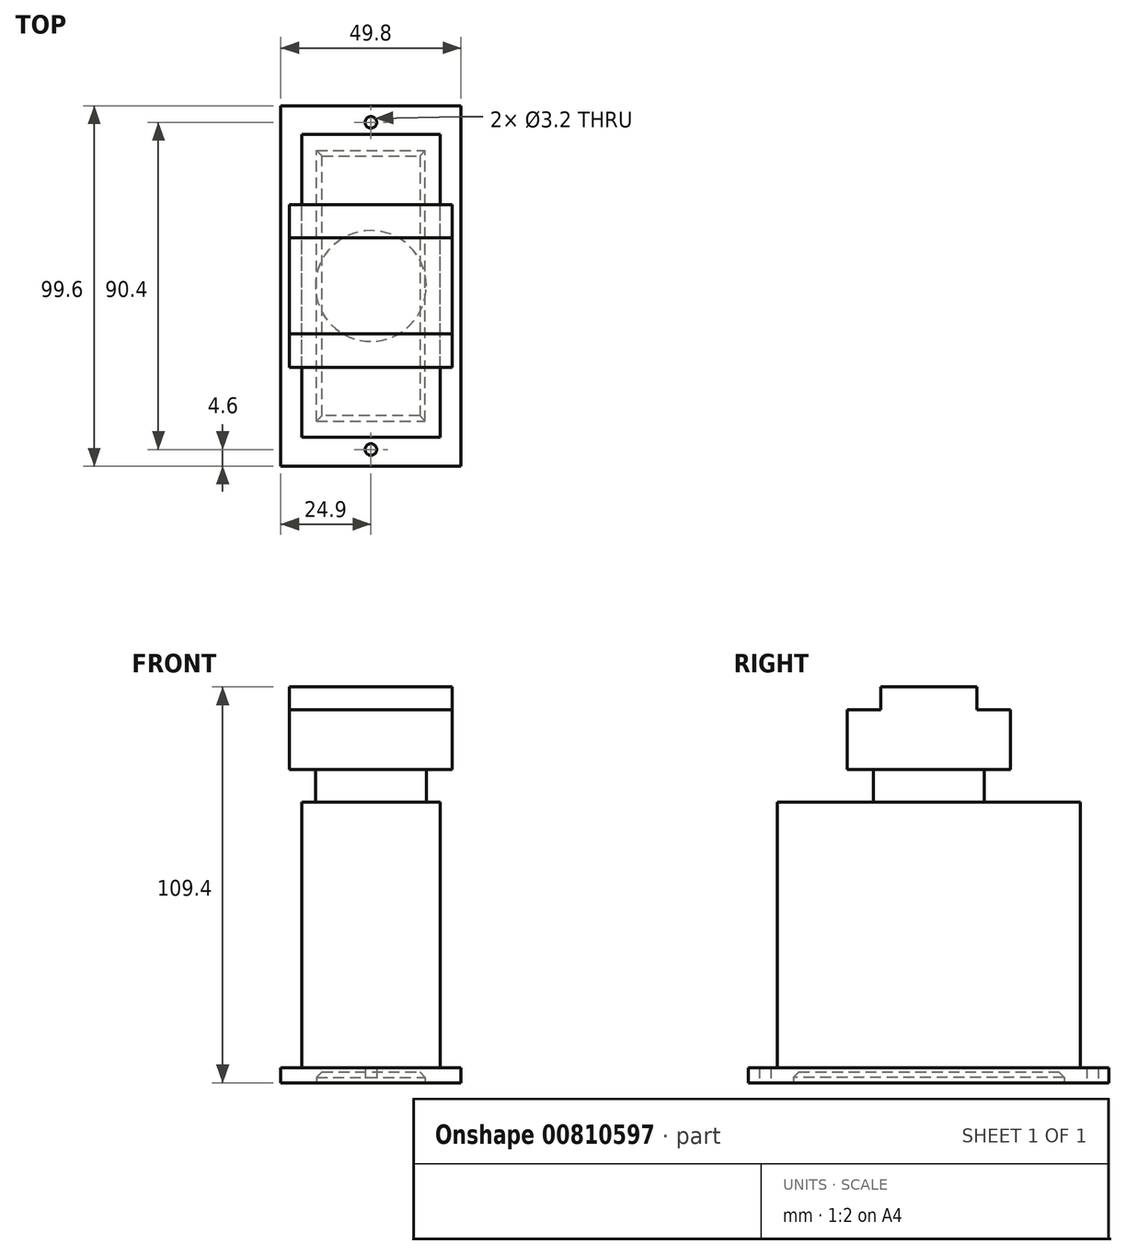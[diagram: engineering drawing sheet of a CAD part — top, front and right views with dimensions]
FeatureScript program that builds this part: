
annotation { "Feature Type Name" : "Feature", "Feature Type Description" : "" }
export const myFeature = defineFeature(function(context is Context, id is Id, definition is map)
    precondition{}
    {
        {
            var Q0;
            Q0=qCreatedBy(makeId("Top.planeOp"),FACE);
            var sketch = newSketch(context, id + "F0", { "sketchPlane" : qUnion([Q0])});
            skLineSegment(sketch, "E0.bottom", {"start": v(24.9, -49.8) * mm, "end": v(-24.9, -49.8) * mm});
            skLineSegment(sketch, "E0.top", {"start": v(24.9, 49.8) * mm, "end": v(-24.9, 49.8) * mm});
            skLineSegment(sketch, "E0.left", {"start": v(24.9, -49.8) * mm, "end": v(24.9, 49.8) * mm});
            skLineSegment(sketch, "E0.right", {"start": v(-24.9, -49.8) * mm, "end": v(-24.9, 49.8) * mm});
            skPoint(sketch, "E0.middle", {"position": v(0, 0) * mm});
            skSolve(sketch);
        }
        {
            var Q0;
            Q0 = qSketchRegion(id + "F0", true);
            extrude(context, id + "F1", {"entities" : qUnion([Q0]), "depth" : 4.2 * mm, "offsetDistance" : 25 * mm});
        }
        {
            var Q0;
            Q0=makeQuery(id+"F1.opExtrude","CAP_FACE",FACE,{"disambiguationData":[OSD([sQuery(id+"F0.wireOp",EDGE,"E0.bottom"),sQuery(id+"F0.wireOp",EDGE,"E0.top"),sQuery(id+"F0.wireOp",EDGE,"E0.left"),sQuery(id+"F0.wireOp",EDGE,"E0.right")])],"isStart":false});
            var sketch = newSketch(context, id + "F2", { "sketchPlane" : qUnion([Q0])});
            skLineSegment(sketch, "E1.bottom", {"start": v(19.12, -41.85) * mm, "end": v(-19.13, -41.85) * mm});
            skLineSegment(sketch, "E1.top", {"start": v(19.13, 41.85) * mm, "end": v(-19.12, 41.85) * mm});
            skLineSegment(sketch, "E1.left", {"start": v(19.12, -41.85) * mm, "end": v(19.13, 41.85) * mm});
            skLineSegment(sketch, "E1.right", {"start": v(-19.13, -41.85) * mm, "end": v(-19.12, 41.85) * mm});
            skPoint(sketch, "E1.middle", {"position": v(0, 0) * mm});
            skSolve(sketch);
        }
        {
            var Q0;
            Q0 = qSketchRegion(id + "F2", true);
            extrude(context, id + "F3", {"entities" : qUnion([Q0]), "operationType" : NewBodyOperationType.ADD, "depth" : 73.4 * mm, "offsetDistance" : 25 * mm});
        }
        {
            var Q0;
            Q0=makeQuery(id+"F3.opExtrude","CAP_FACE",FACE,{"disambiguationData":[OSD([sQuery(id+"F2.wireOp",EDGE,"E1.bottom"),sQuery(id+"F2.wireOp",EDGE,"E1.top"),sQuery(id+"F2.wireOp",EDGE,"E1.left"),sQuery(id+"F2.wireOp",EDGE,"E1.right")])],"isStart":false});
            var sketch = newSketch(context, id + "F4", { "sketchPlane" : qUnion([Q0])});
            skCircle(sketch, "E2", {"center": v(0, 0) * mm, "radius": 15.3 * mm});
            skSolve(sketch);
        }
        {
            var Q0;
            Q0 = qSketchRegion(id + "F4", true);
            extrude(context, id + "F5", {"entities" : qUnion([Q0]), "operationType" : NewBodyOperationType.ADD, "depth" : 9 * mm, "offsetDistance" : 25 * mm});
        }
        {
            var Q0;
            Q0=makeQuery(id+"F5.opExtrude","CAP_FACE",FACE,{"disambiguationData":[OSD([sQuery(id+"F4.wireOp",EDGE,"E2")])],"isStart":false});
            var sketch = newSketch(context, id + "F6", { "sketchPlane" : qUnion([Q0])});
            skLineSegment(sketch, "E3.bottom", {"start": v(22.5, -22.5) * mm, "end": v(-22.5, -22.5) * mm});
            skLineSegment(sketch, "E3.top", {"start": v(22.5, 22.5) * mm, "end": v(-22.5, 22.5) * mm});
            skLineSegment(sketch, "E3.left", {"start": v(22.5, -22.5) * mm, "end": v(22.5, 22.5) * mm});
            skLineSegment(sketch, "E3.right", {"start": v(-22.5, -22.5) * mm, "end": v(-22.5, 22.5) * mm});
            skPoint(sketch, "E3.middle", {"position": v(0, 0) * mm});
            skSolve(sketch);
        }
        {
            var Q0;
            Q0 = qSketchRegion(id + "F6", true);
            extrude(context, id + "F7", {"entities" : qUnion([Q0]), "depth" : 16.5 * mm, "offsetDistance" : 25 * mm});
        }
        {
            var Q0;
            Q0=makeQuery(id+"F7.opExtrude","CAP_FACE",FACE,{"disambiguationData":[OSD([sQuery(id+"F6.wireOp",EDGE,"E3.bottom"),sQuery(id+"F6.wireOp",EDGE,"E3.top"),sQuery(id+"F6.wireOp",EDGE,"E3.left"),sQuery(id+"F6.wireOp",EDGE,"E3.right")])],"isStart":false});
            var sketch = newSketch(context, id + "F8", { "sketchPlane" : qUnion([Q0])});
            skLineSegment(sketch, "E4.bottom", {"start": v(22.5, -13.25) * mm, "end": v(-22.5, -13.25) * mm});
            skLineSegment(sketch, "E4.top", {"start": v(22.5, 13.25) * mm, "end": v(-22.5, 13.25) * mm});
            skLineSegment(sketch, "E4.left", {"start": v(22.5, -13.25) * mm, "end": v(22.5, 13.25) * mm});
            skLineSegment(sketch, "E4.right", {"start": v(-22.5, -13.25) * mm, "end": v(-22.5, 13.25) * mm});
            skPoint(sketch, "E4.middle", {"position": v(0, 0) * mm});
            skSolve(sketch);
        }
        {
            var Q0;
            Q0 = qSketchRegion(id + "F8", true);
            extrude(context, id + "F9", {"entities" : qUnion([Q0]), "operationType" : NewBodyOperationType.ADD, "depth" : 6.3 * mm, "offsetDistance" : 25 * mm});
        }
        {
            var Q0;
            Q0=makeQuery(id+"F1.opExtrude","CAP_FACE",FACE,{"disambiguationData":[OSD([sQuery(id+"F0.wireOp",EDGE,"E0.bottom"),sQuery(id+"F0.wireOp",EDGE,"E0.top"),sQuery(id+"F0.wireOp",EDGE,"E0.left"),sQuery(id+"F0.wireOp",EDGE,"E0.right")])],"isStart":true});
            var sketch = newSketch(context, id + "F10", { "sketchPlane" : qUnion([Q0])});
            skLineSegment(sketch, "E5.bottom", {"start": v(-15, 37.4) * mm, "end": v(15, 37.4) * mm});
            skLineSegment(sketch, "E5.top", {"start": v(-15, -37.4) * mm, "end": v(15, -37.4) * mm});
            skLineSegment(sketch, "E5.left", {"start": v(-15, 37.4) * mm, "end": v(-15, -37.4) * mm});
            skLineSegment(sketch, "E5.right", {"start": v(15, 37.4) * mm, "end": v(15, -37.4) * mm});
            skPoint(sketch, "E5.middle", {"position": v(0, 0) * mm});
            skSolve(sketch);
        }
        {
            var Q0;
            Q0 = qSketchRegion(id + "F10", true);
            extrude(context, id + "F11", {"entities" : qUnion([Q0]), "operationType" : NewBodyOperationType.REMOVE, "oppositeDirection" : true, "depth" : 3 * mm, "offsetDistance" : 25 * mm});
        }
        {
            var Q0;
            Q0=makeQuery(id+"F1.opExtrude","CAP_FACE",FACE,{"disambiguationData":[OSD([sQuery(id+"F0.wireOp",EDGE,"E0.bottom"),sQuery(id+"F0.wireOp",EDGE,"E0.top"),sQuery(id+"F0.wireOp",EDGE,"E0.left"),sQuery(id+"F0.wireOp",EDGE,"E0.right")])],"isStart":true});
            var sketch = newSketch(context, id + "F12", { "sketchPlane" : qUnion([Q0])});
            skCircle(sketch, "E6", {"center": v(0, -45.2) * mm, "radius": 1.6 * mm});
            skCircle(sketch, "E7", {"center": v(0, 45.2) * mm, "radius": 1.6 * mm});
            skSolve(sketch);
        }
        {
            var Q0;
            Q0 = qSketchRegion(id + "F12", true);
            extrude(context, id + "F13", {"entities" : qUnion([Q0]), "operationType" : NewBodyOperationType.REMOVE, "oppositeDirection" : true, "depth" : 25 * mm, "offsetDistance" : 25 * mm});
        }
        {
            var Q0;
            Q0=makeQuery(id+"F13.boolean.opBoolean","COPY",EDGE,{"derivedFrom":makeQuery(id+"F13.opExtrude","CAP_EDGE",EDGE,{"disambiguationData":[OSD([sQuery(id+"F12.wireOp",EDGE,"E6")])],"isStart":true})});
            var Q1;
            Q1=makeQuery(id+"F13.boolean.opBoolean","COPY",EDGE,{"derivedFrom":makeQuery(id+"F13.opExtrude","CAP_EDGE",EDGE,{"disambiguationData":[OSD([sQuery(id+"F12.wireOp",EDGE,"E7")])],"isStart":true})});
            var Q2;
            Q2=makeQuery(id+"F11.boolean.opBoolean","COPY",FACE,{"derivedFrom":makeQuery(id+"F11.opExtrude","CAP_FACE",FACE,{"disambiguationData":[OSD([sQuery(id+"F10.wireOp",EDGE,"E5.bottom"),sQuery(id+"F10.wireOp",EDGE,"E5.top"),sQuery(id+"F10.wireOp",EDGE,"E5.left"),sQuery(id+"F10.wireOp",EDGE,"E5.right")])],"isStart":false})});
            chamfer(context, id + "F14", {"entities" : qUnion([Q0, Q1, Q2]), "width" : 1.5 * mm, "tangentPropagation" : true});
        }
    });
